# Revit family: ARKOSLIGHT_Track Black Foster Micro Custom Surface
name_source: partatom
category: Lighting Fixtures
units: mm (PartAtom-declared; Revit-internal decimal feet)

## family parameters
Cut with Voids When Loaded = No
Host = Face
Light Source = No
Part Type = Normal
Room Calculation Point = No
Round Connector Dimension = Use Diameter
Shared = No

## types (2) — shared parameters
ARKOSLIGHT_Dimming = Yes
ARKOSLIGHT_Fixture Type = ACCESSORIES
ARKOSLIGHT_Model = ACCESSORIES
ARKOSLIGHT_Series = BLACK FOSTER MICRO CUSTOM SURFACE ACCESSORIES
Apparent Load = 4 VA
Description = Select the number and length of profiles suitable for the defined length. End cap kit not included
Manufacturer = ARKOSLIGHT
Model = ACCESSORIES
URL = https://www.arkoslight.com
zero-valued in all types: Default Elevation

## per-type parameters (varying)
| type | ARKOSLIGHT_Body Color | ARKOSLIGHT_Color | ARKOSLIGHT_Reference |
| A4500X00NT - BLACK FOSTER MICRO CUSTOM SURFACE XM NT | ARKOSLIGHT_Textured black | Textured black | A4500X00NT |
| A4500X00WT - BLACK FOSTER MICRO CUSTOM SURFACE XM WT | ARKOSLIGHT_Textured white | Textured white | A4500X00WT |

## geometry (parser evidence)
native form markers: Sweep x2
no freeform markers — native parametric forms only
